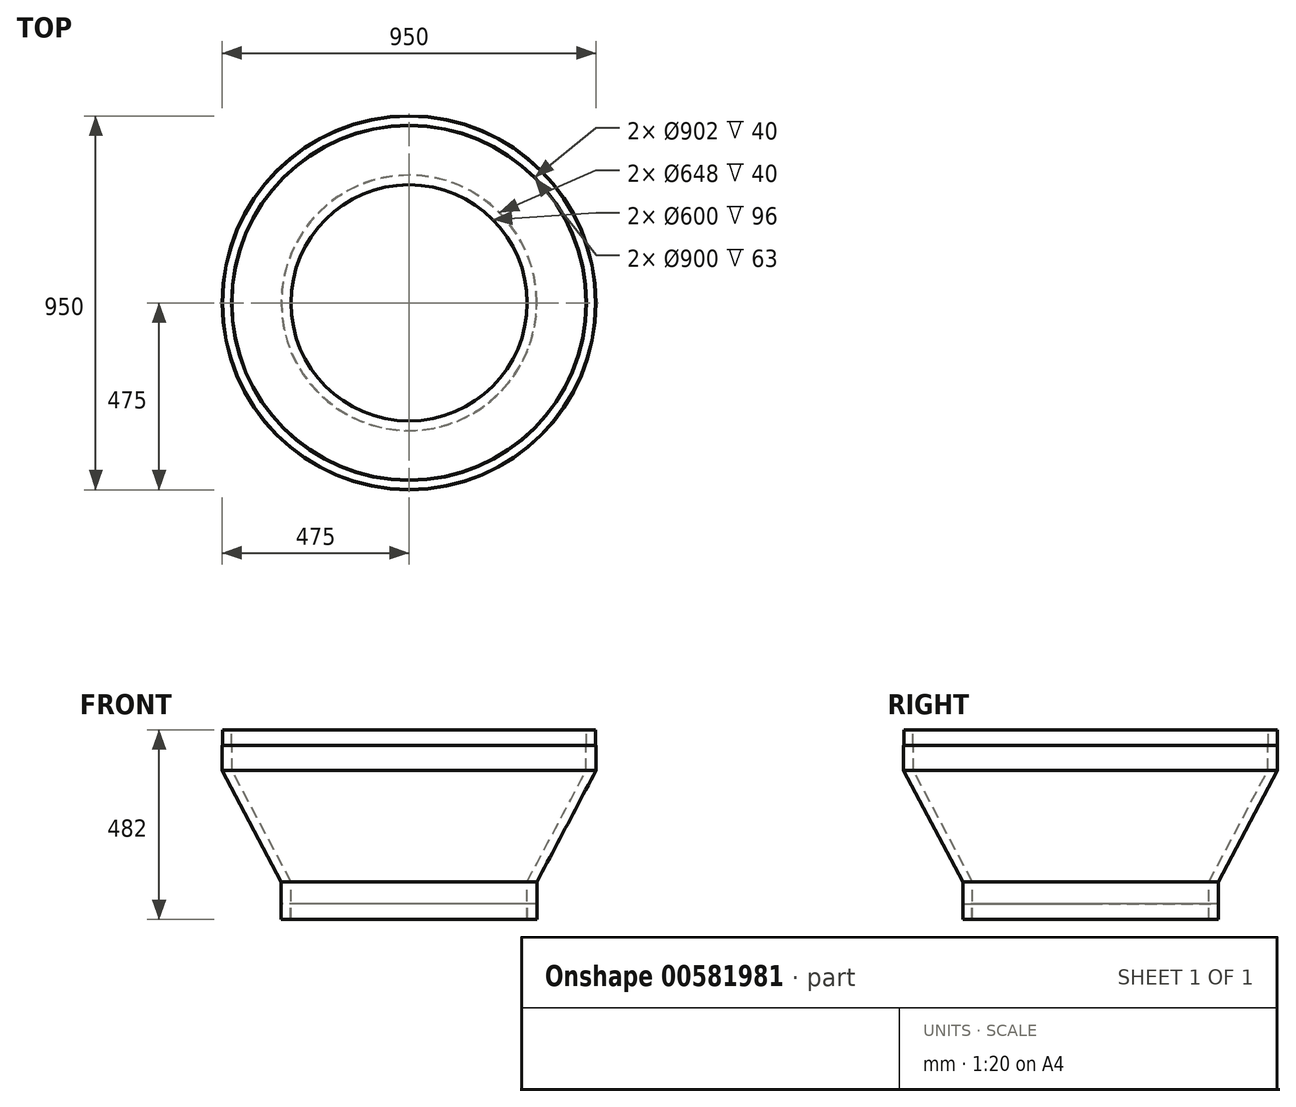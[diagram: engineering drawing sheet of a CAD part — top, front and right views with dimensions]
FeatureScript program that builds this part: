
annotation { "Feature Type Name" : "Feature", "Feature Type Description" : "" }
export const myFeature = defineFeature(function(context is Context, id is Id, definition is map)
    precondition{}
    {
        {
            var Q0;
            Q0=qCreatedBy(makeId("Front.planeOp"),FACE);
            var sketch = newSketch(context, id + "F0", { "sketchPlane" : qUnion([Q0])});
            skLineSegment(sketch, "E0", {"start": v(0, 433.08) * mm, "end": v(0, -434.74) * mm, "construction": true});
            skLineSegment(sketch, "E1", {"start": v(-300, -248.87) * mm, "end": v(-300, -152.87) * mm});
            skLineSegment(sketch, "E2", {"start": v(-300, -248.87) * mm, "end": v(-301, -248.87) * mm});
            skLineSegment(sketch, "E3", {"start": v(-301, -248.87) * mm, "end": v(-301, -208.87) * mm});
            skLineSegment(sketch, "E4", {"start": v(-301, -208.87) * mm, "end": v(-324, -208.87) * mm});
            skLineSegment(sketch, "E5", {"start": v(-324, -208.87) * mm, "end": v(-324, -248.87) * mm});
            skLineSegment(sketch, "E6", {"start": v(-324, -248.87) * mm, "end": v(-325, -248.87) * mm});
            skLineSegment(sketch, "E7", {"start": v(-325, -248.87) * mm, "end": v(-325, -152.87) * mm});
            skLineSegment(sketch, "E8", {"start": v(-474, 233.13) * mm, "end": v(-451, 233.13) * mm});
            skLineSegment(sketch, "E9", {"start": v(-451, 233.13) * mm, "end": v(-451, 193.13) * mm});
            skLineSegment(sketch, "E10", {"start": v(-451, 193.13) * mm, "end": v(-450, 193.13) * mm});
            skLineSegment(sketch, "E11", {"start": v(-450, 193.13) * mm, "end": v(-450, 130.13) * mm});
            skLineSegment(sketch, "E12", {"start": v(-474, 233.13) * mm, "end": v(-474, 193.13) * mm});
            skLineSegment(sketch, "E13", {"start": v(-474, 193.13) * mm, "end": v(-475, 193.13) * mm});
            skLineSegment(sketch, "E14", {"start": v(-475, 193.13) * mm, "end": v(-475, 130.13) * mm});
            skLineSegment(sketch, "E15", {"start": v(-450, 130.13) * mm, "end": v(-300, -152.87) * mm});
            skLineSegment(sketch, "E16", {"start": v(-475, 130.13) * mm, "end": v(-325, -152.87) * mm});
            skSolve(sketch);
        }
        {
            var Q0;
            Q0=qSketchRegion(id+"F0",true);
            var Q1;
            Q1=sQuery(id+"F0.wireOp",EDGE,"E0");
            revolve(context, id + "F1", {"entities" : qUnion([Q0]), "axis" : qUnion([Q1]), "revolveType" : RevolveType.FULL});
        }
    });
